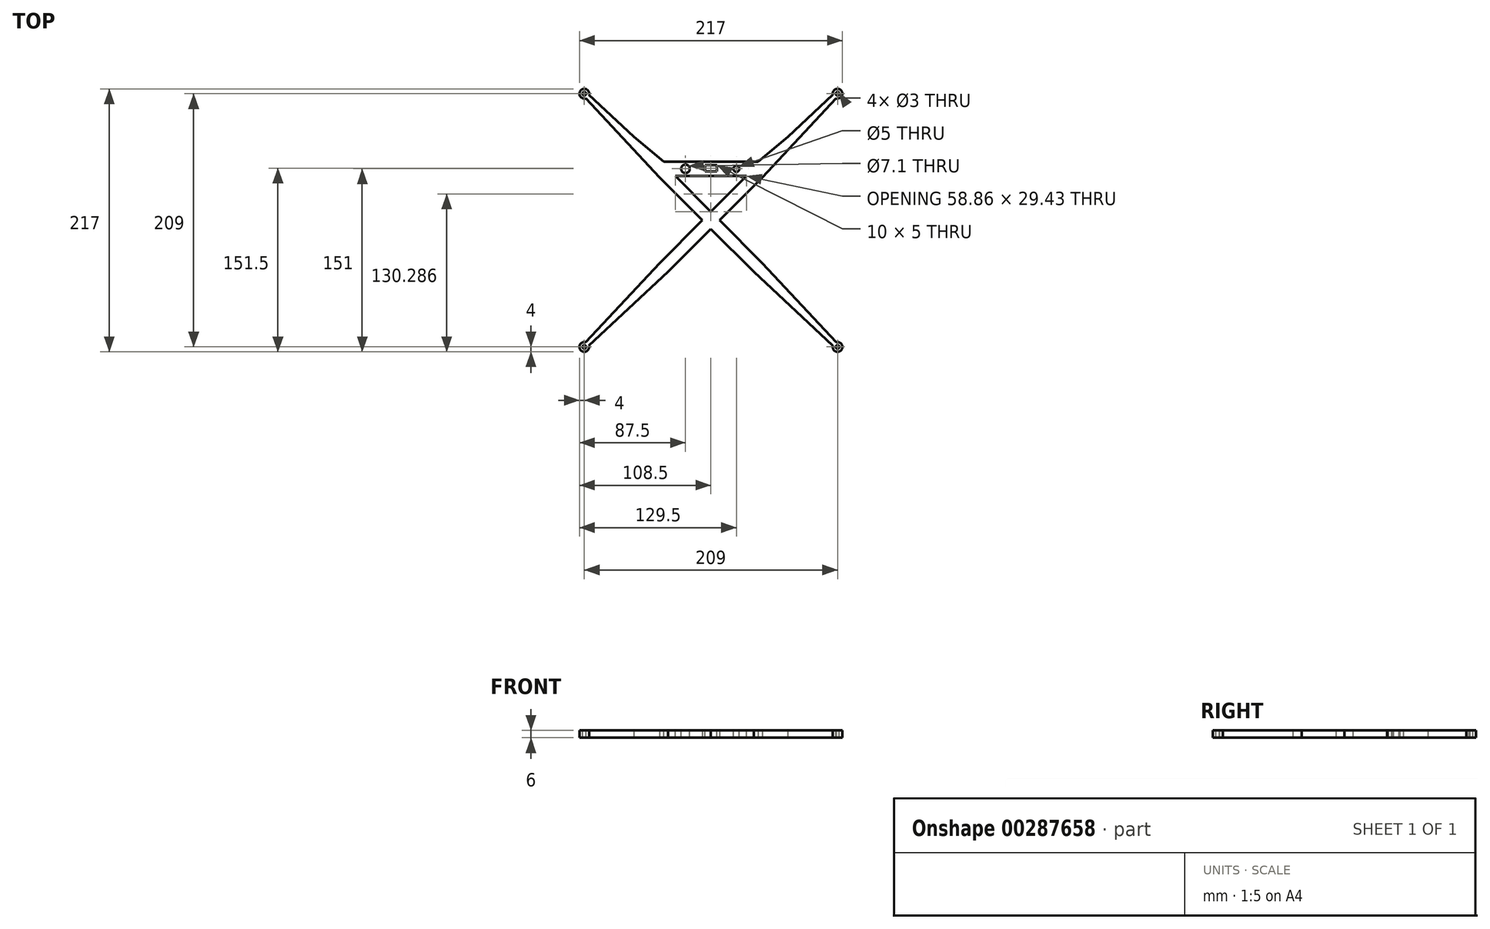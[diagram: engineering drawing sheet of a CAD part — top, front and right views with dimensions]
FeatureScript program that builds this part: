
annotation { "Feature Type Name" : "Feature", "Feature Type Description" : "" }
export const myFeature = defineFeature(function(context is Context, id is Id, definition is map)
    precondition{}
    {
        {
            var Q0;
            Q0=qCreatedBy(makeId("Top.planeOp"),FACE);
            var sketch = newSketch(context, id + "F0", { "sketchPlane" : qUnion([Q0])});
            skCircle(sketch, "E0", {"center": v(-104.5, 104.5) * mm, "radius": 4 * mm});
            skSolve(sketch);
        }
        {
            var Q0;
            Q0=qSketchRegion(id+"F0",true);
            extrude(context, id + "F1", {"entities" : qUnion([Q0]), "depth" : 6 * mm, "offsetDistance" : 25 * mm});
        }
        {
            var Q0;
            Q0=qCreatedBy(makeId("Top.planeOp"),FACE);
            var sketch = newSketch(context, id + "F2", { "sketchPlane" : qUnion([Q0])});
            skLineSegment(sketch, "E1", {"start": v(0, 0) * mm, "end": v(0, 7.07) * mm});
            skLineSegment(sketch, "E2", {"start": v(-100.64, 103.46) * mm, "end": v(-103.46, 100.64) * mm});
            skLineSegment(sketch, "E3", {"start": v(-103.46, 100.64) * mm, "end": v(-42.43, 35.36) * mm});
            skLineSegment(sketch, "E4", {"start": v(-42.43, 35.36) * mm, "end": v(-7.07, 0) * mm});
            skLineSegment(sketch, "E5", {"start": v(-7.07, 0) * mm, "end": v(0, 0) * mm});
            skLineSegment(sketch, "E6", {"start": v(-100.64, 103.46) * mm, "end": v(-35.36, 42.43) * mm});
            skLineSegment(sketch, "E7", {"start": v(-35.36, 42.43) * mm, "end": v(0, 7.07) * mm});
            skLineSegment(sketch, "E8", {"start": v(0, 0) * mm, "end": v(-104.5, 104.5) * mm, "construction": true});
            skSolve(sketch);
        }
        {
            var Q0;
            Q0=qSketchRegion(id+"F2",true);
            var Q1;
            Q1=makeQuery(id+"F1.opExtrude","CAP_FACE",FACE,{"disambiguationData":[OSD([sQuery(id+"F0.wireOp",EDGE,"E0")])],"isStart":false});
            extrude(context, id + "F3", {"entities" : qUnion([Q0]), "operationType" : NewBodyOperationType.ADD, "endBound" : BoundingType.UP_TO_SURFACE, "depth" : 25 * mm, "endBoundEntityFace" : qUnion([Q1]), "offsetDistance" : 25 * mm});
        }
        {
            var Q0;
            {var subQ0=sQuery(id+"F0.wireOp",EDGE,"E0");Q0=makeQuery(id+"F3.boolean.opBoolean","MERGE",FACE,{"derivedFrom":[makeQuery(id+"F1.opExtrude","CAP_FACE",FACE,{"disambiguationData":[OSD([subQ0])],"isStart":false}),makeQuery(id+"F3.opExtrude","CAP_FACE",FACE,{"disambiguationData":[OSD([subQ0])],"isStart":false})]});}
            var sketch = newSketch(context, id + "F4", { "sketchPlane" : qUnion([Q0])});
            skCircle(sketch, "E9", {"center": v(-104.5, 104.5) * mm, "radius": 1.5 * mm});
            skSolve(sketch);
        }
        {
            var Q0;
            Q0=qSketchRegion(id+"F4",true);
            extrude(context, id + "F5", {"entities" : qUnion([Q0]), "operationType" : NewBodyOperationType.REMOVE, "endBound" : BoundingType.THROUGH_ALL, "oppositeDirection" : true, "depth" : 25 * mm, "offsetDistance" : 25 * mm});
        }
        {
            var Q0;
            Q0=makeQuery(id+"F1.opExtrude","SWEPT_BODY",BODY,{"disambiguationData":[OSD([sQuery(id+"F0.wireOp",EDGE,"E0")])]});
            var Q1;
            Q1=makeQuery(id+"F3.opExtrude","SWEPT_EDGE",EDGE,{"disambiguationData":[OSD([sQuery(id+"F2.wireOp",EDGE,"E1"),sQuery(id+"F2.wireOp",EDGE,"E5")])]});
            circularPattern(context, id + "F6", {"entities" : qUnion([Q0]), "axis" : qUnion([Q1]), "angle" : 360 * degree, "instanceCount" : 4, "equalSpace" : true});
        }
        {
            var Q0;
            Q0=makeQuery(id+"F1.opExtrude","SWEPT_BODY",BODY,{"disambiguationData":[OSD([sQuery(id+"F0.wireOp",EDGE,"E0")])]});
            var Q1;
            Q1=makeQuery(id+"F6.opPattern","COPY",BODY,{"derivedFrom":makeQuery(id+"F1.opExtrude","SWEPT_BODY",BODY,{"disambiguationData":[OSD([sQuery(id+"F0.wireOp",EDGE,"E0")])]}),"instanceName":"1"});
            var Q2;
            Q2=makeQuery(id+"F6.opPattern","COPY",BODY,{"derivedFrom":makeQuery(id+"F1.opExtrude","SWEPT_BODY",BODY,{"disambiguationData":[OSD([sQuery(id+"F0.wireOp",EDGE,"E0")])]}),"instanceName":"2"});
            var Q3;
            Q3=makeQuery(id+"F6.opPattern","COPY",BODY,{"derivedFrom":makeQuery(id+"F1.opExtrude","SWEPT_BODY",BODY,{"disambiguationData":[OSD([sQuery(id+"F0.wireOp",EDGE,"E0")])]}),"instanceName":"3"});
            booleanBodies(context, id + "F7", {"operationType" : BooleanOperationType.UNION, "tools" : qUnion([Q0, Q1, Q2, Q3])});
        }
        {
            var Q0;
            Q0=qCreatedBy(makeId("Top.planeOp"),FACE);
            var sketch = newSketch(context, id + "F8", { "sketchPlane" : qUnion([Q0])});
            skLineSegment(sketch, "E10.bottom", {"start": v(-42.5, 36.5) * mm, "end": v(42.5, 36.5) * mm});
            skLineSegment(sketch, "E10.top", {"start": v(-42.5, 48.5) * mm, "end": v(42.5, 48.5) * mm});
            skLineSegment(sketch, "E10.left", {"start": v(-42.5, 36.5) * mm, "end": v(-42.5, 48.5) * mm});
            skLineSegment(sketch, "E10.right", {"start": v(42.5, 36.5) * mm, "end": v(42.5, 48.5) * mm});
            skPoint(sketch, "E10.middle", {"position": v(0, 42.5) * mm});
            skSolve(sketch);
        }
        {
            var Q0;
            Q0=qSketchRegion(id+"F8",true);
            var Q1;
            {var subQ0=sQuery(id+"F0.wireOp",EDGE,"E0");Q1=makeQuery(id+"F3.boolean.opBoolean","MERGE",FACE,{"derivedFrom":[makeQuery(id+"F1.opExtrude","CAP_FACE",FACE,{"disambiguationData":[OSD([subQ0])],"isStart":false}),makeQuery(id+"F3.opExtrude","CAP_FACE",FACE,{"disambiguationData":[OSD([subQ0])],"isStart":false})]});}
            extrude(context, id + "F9", {"entities" : qUnion([Q0]), "operationType" : NewBodyOperationType.ADD, "endBound" : BoundingType.UP_TO_SURFACE, "depth" : 25 * mm, "endBoundEntityFace" : qUnion([Q1]), "offsetDistance" : 25 * mm});
        }
        {
            var Q0;
            {var subQ0=sQuery(id+"F0.wireOp",EDGE,"E0");var subQ1=makeQuery(id+"F3.boolean.opBoolean","MERGE",FACE,{"derivedFrom":[makeQuery(id+"F1.opExtrude","CAP_FACE",FACE,{"disambiguationData":[OSD([subQ0])],"isStart":false}),makeQuery(id+"F3.opExtrude","CAP_FACE",FACE,{"disambiguationData":[OSD([subQ0])],"isStart":false})]});Q0=makeQuery(id+"F9.boolean.opBoolean","MERGE",FACE,{"derivedFrom":[makeQuery(id+"F7.opBoolean","MERGE",FACE,{"derivedFrom":[subQ1,makeQuery(id+"F6.opPattern","COPY",FACE,{"derivedFrom":subQ1,"instanceName":"1"}),makeQuery(id+"F6.opPattern","COPY",FACE,{"derivedFrom":subQ1,"instanceName":"2"}),makeQuery(id+"F6.opPattern","COPY",FACE,{"derivedFrom":subQ1,"instanceName":"3"})]}),makeQuery(id+"F9.opExtrude","CAP_FACE",FACE,{"disambiguationData":[OSD([subQ0])],"isStart":false})]});}
            var sketch = newSketch(context, id + "F10", { "sketchPlane" : qUnion([Q0])});
            skCircle(sketch, "E11", {"center": v(-21, 42.5) * mm, "radius": 3.55 * mm});
            skCircle(sketch, "E12", {"center": v(21, 42.5) * mm, "radius": 2.5 * mm});
            skLineSegment(sketch, "E13.bottom", {"start": v(5, 40.5) * mm, "end": v(-5, 40.5) * mm});
            skLineSegment(sketch, "E13.top", {"start": v(5, 45.5) * mm, "end": v(-5, 45.5) * mm});
            skLineSegment(sketch, "E13.left", {"start": v(5, 40.5) * mm, "end": v(5, 45.5) * mm});
            skLineSegment(sketch, "E13.right", {"start": v(-5, 40.5) * mm, "end": v(-5, 45.5) * mm});
            skPoint(sketch, "E13.middle", {"position": v(0, 43) * mm});
            skSolve(sketch);
        }
        {
            var Q0;
            Q0=qSketchRegion(id+"F10",true);
            extrude(context, id + "F11", {"entities" : qUnion([Q0]), "operationType" : NewBodyOperationType.REMOVE, "endBound" : BoundingType.THROUGH_ALL, "oppositeDirection" : true, "depth" : 25 * mm, "offsetDistance" : 25 * mm});
        }
        {
            var Q0;
            Q0=makeQuery(id+"F9.boolean.opBoolean","INTERSECT",EDGE,{"derivedFrom":[makeQuery(id+"F3.opExtrude","SWEPT_FACE",FACE,{"disambiguationData":[OSD([sQuery(id+"F2.wireOp",EDGE,"E6")])]}),makeQuery(id+"F9.opExtrude","SWEPT_FACE",FACE,{"disambiguationData":[OSD([sQuery(id+"F8.wireOp",EDGE,"E10.top")])]})]});
            var Q1;
            Q1=makeQuery(id+"F9.boolean.opBoolean","INTERSECT",EDGE,{"derivedFrom":[makeQuery(id+"F6.opPattern","COPY",FACE,{"derivedFrom":makeQuery(id+"F3.opExtrude","SWEPT_FACE",FACE,{"disambiguationData":[OSD([sQuery(id+"F2.wireOp",EDGE,"E3")])]}),"instanceName":"1"}),makeQuery(id+"F9.opExtrude","SWEPT_FACE",FACE,{"disambiguationData":[OSD([sQuery(id+"F8.wireOp",EDGE,"E10.top")])]})]});
            chamfer(context, id + "F12", {"entities" : qUnion([Q0, Q1]), "chamferType" : ChamferType.TWO_OFFSETS, "width1" : 3 * mm, "oppositeDirection" : false, "width2" : 30 * mm, "tangentPropagation" : true});
        }
    });
